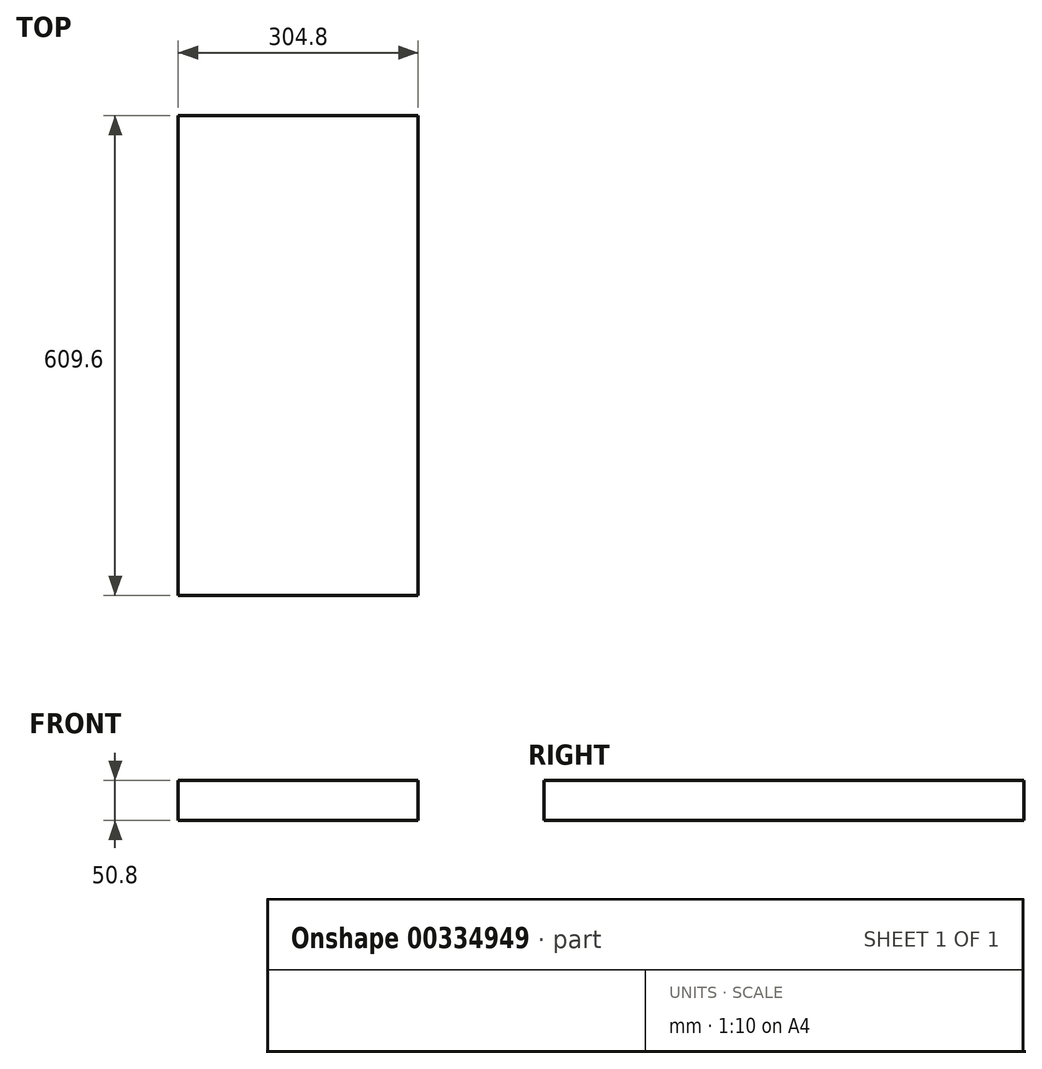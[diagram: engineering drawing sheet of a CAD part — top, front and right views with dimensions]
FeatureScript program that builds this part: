
annotation { "Feature Type Name" : "Feature", "Feature Type Description" : "" }
export const myFeature = defineFeature(function(context is Context, id is Id, definition is map)
    precondition{}
    {
        {
            var Q0;
            Q0=qCreatedBy(makeId("Top.planeOp"),FACE);
            var sketch = newSketch(context, id + "F0", { "sketchPlane" : qUnion([Q0])});
            skLineSegment(sketch, "E0", {"start": v(-296.93, 448.55) * mm, "end": v(7.87, 448.55) * mm});
            skLineSegment(sketch, "E1", {"start": v(7.87, 448.55) * mm, "end": v(7.87, -161.05) * mm});
            skLineSegment(sketch, "E2", {"start": v(7.87, -161.05) * mm, "end": v(-296.93, -161.05) * mm});
            skLineSegment(sketch, "E3", {"start": v(-296.93, -161.05) * mm, "end": v(-296.93, 448.55) * mm});
            skSolve(sketch);
        }
        {
            var Q0;
            Q0=makeQuery(id+"F0.imprint","IMPRINT",FACE,{"disambiguationData":[TD([[makeQuery(id+"F0.imprint","IMPRINT",EDGE,{"derivedFrom":sQuery(id+"F0.wireOp",EDGE,"E0")}),-1.0]])]});
            extrude(context, id + "F1", {"entities" : qUnion([Q0]), "depth" : 50.8 * mm});
        }
    });
